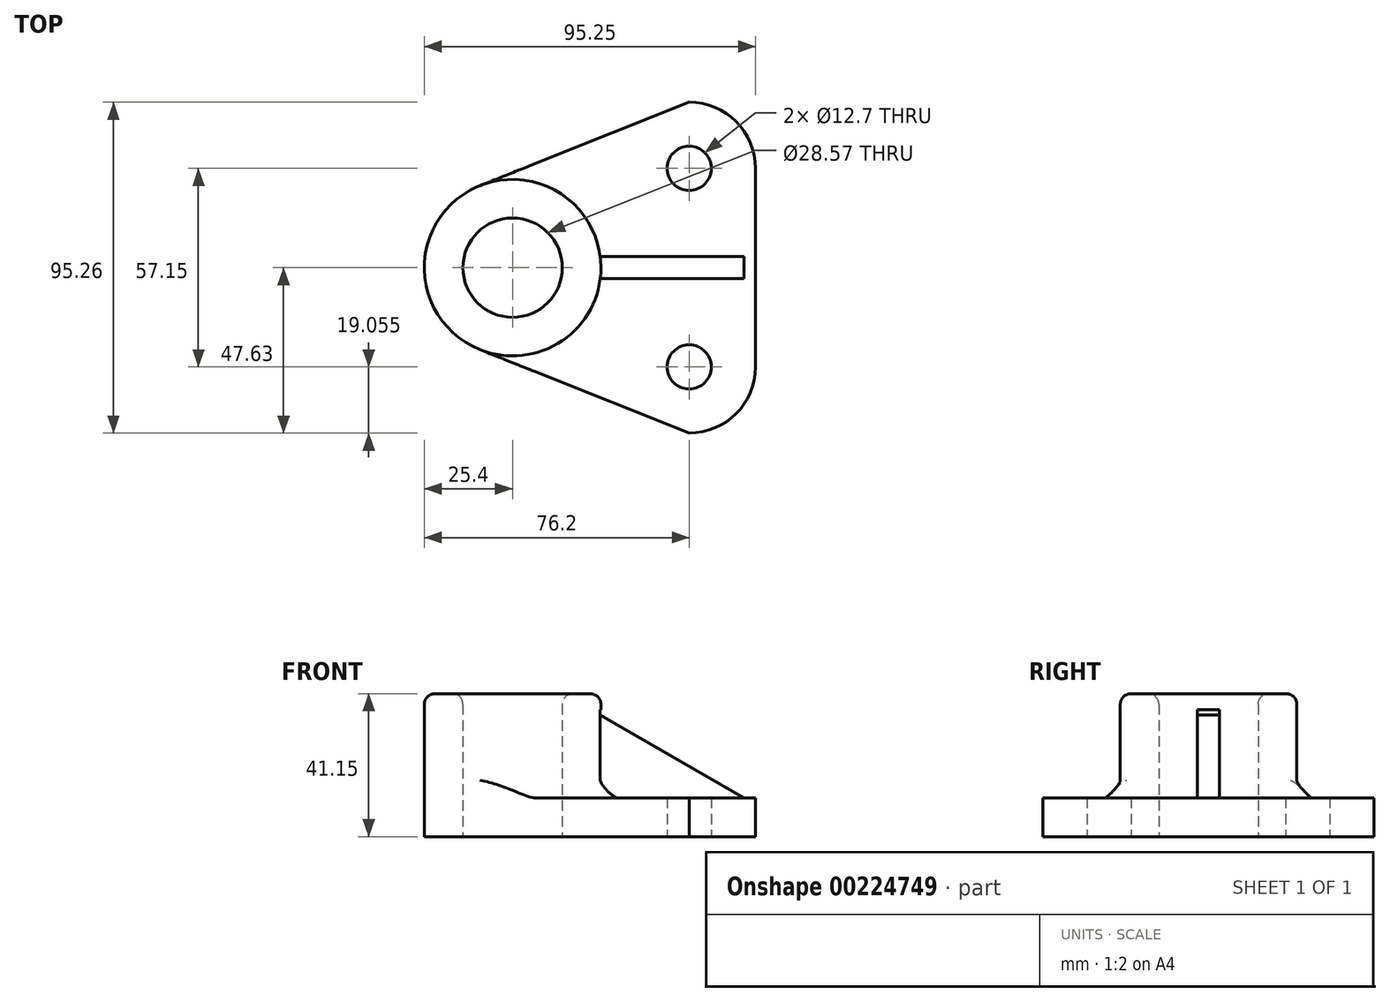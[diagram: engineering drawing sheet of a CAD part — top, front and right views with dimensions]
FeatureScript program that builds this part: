
annotation { "Feature Type Name" : "Feature", "Feature Type Description" : "" }
export const myFeature = defineFeature(function(context is Context, id is Id, definition is map)
    precondition{}
    {
        {
            var Q0;
            Q0=qCreatedBy(makeId("Top.planeOp"),FACE);
            var sketch = newSketch(context, id + "F0", { "sketchPlane" : qUnion([Q0])});
            skCircle(sketch, "E0", {"center": v(0, 0) * mm, "radius": 25.4 * mm});
            skCircle(sketch, "E1", {"center": v(50.8, -28.58) * mm, "radius": 6.35 * mm});
            skCircle(sketch, "E2", {"center": v(50.8, 28.57) * mm, "radius": 6.35 * mm});
            skArc(sketch, "E3", {"start": v(69.85, 28.57) * mm, "mid": v(64.27, 42.05) * mm, "end": v(50.8, 47.62) * mm});
            skArc(sketch, "E4", {"start": v(50.8, -47.62) * mm, "mid": v(64.27, -42.05) * mm, "end": v(69.85, -28.58) * mm});
            skLineSegment(sketch, "E5", {"start": v(69.85, 28.57) * mm, "end": v(69.85, -28.58) * mm});
            skLineSegment(sketch, "E6", {"start": v(0, 0) * mm, "end": v(0, 25.4) * mm});
            skLineSegment(sketch, "E7", {"start": v(0, 0) * mm, "end": v(0, -25.4) * mm});
            skLineSegment(sketch, "E8", {"start": v(50.8, 47.62) * mm, "end": v(-9.42, 23.6) * mm});
            skLineSegment(sketch, "E9", {"start": v(50.8, -47.63) * mm, "end": v(-9.42, -23.6) * mm});
            skCircle(sketch, "E10", {"center": v(0, 0) * mm, "radius": 14.29 * mm});
            skLineSegment(sketch, "E11", {"start": v(69.85, 0) * mm, "end": v(66.55, 0) * mm});
            skPoint(sketch, "E11.endSnap0", {"position": v(69.85, 0) * mm});
            skLineSegment(sketch, "E12.right", {"start": v(108.5, -2.46) * mm, "end": v(108.5, 2.46) * mm});
            skPoint(sketch, "E12.middle", {"position": v(66.55, 0) * mm});
            skPoint(sketch, "E13.orphan", {"position": v(24.6, -2.46) * mm});
            skPoint(sketch, "E14.orphan", {"position": v(24.6, 2.46) * mm});
            skSolve(sketch);
        }
        {
            var Q0;
            {var subQ0=sQuery(id+"F0.wireOp",EDGE,"E6");var subQ1=sQuery(id+"F0.wireOp",EDGE,"E0");var subQ2=makeQuery(id+"F0.imprint","INTERSECT",VERTEX,{"derivedFrom":[subQ1,subQ0]});Q0=makeQuery(id+"F0.imprint","IMPRINT",FACE,{"disambiguationData":[TD([[makeQuery(id+"F0.imprint","IMPRINT",EDGE,{"disambiguationData":[TD([[subQ2,-1.0]])],"derivedFrom":subQ1}),1.0]])]});}
            var Q1;
            {var subQ0=sQuery(id+"F0.wireOp",EDGE,"E6");var subQ1=sQuery(id+"F0.wireOp",EDGE,"E0");var subQ2=makeQuery(id+"F0.imprint","INTERSECT",VERTEX,{"derivedFrom":[subQ1,subQ0]});Q1=makeQuery(id+"F0.imprint","IMPRINT",FACE,{"disambiguationData":[TD([[makeQuery(id+"F0.imprint","IMPRINT",EDGE,{"disambiguationData":[TD([[subQ2,1.0]])],"derivedFrom":subQ1}),1.0]])]});}
            extrude(context, id + "F1", {"entities" : qUnion([Q0, Q1]), "depth" : 41.15 * mm});
        }
        {
            var Q0;
            Q0 = qSketchRegion(id + "F0", true);
            extrude(context, id + "F2", {"entities" : qUnion([Q0]), "operationType" : NewBodyOperationType.ADD, "depth" : 11.18 * mm});
        }
        {
            var Q0;
            Q0=makeQuery(id+"F1.opExtrude","CAP_FACE",FACE,{"disambiguationData":[OSD([sQuery(id+"F0.wireOp",EDGE,"E0"),sQuery(id+"F0.wireOp",EDGE,"E10")])],"isStart":false});
            fillet(context, id + "F3", {"entities" : qUnion([Q0]), "radius" : 3.05 * mm, "tangentPropagation" : true, "allowEdgeOverflow" : false});
        }
        {
            var Q0;
            Q0=makeQuery(id+"F2.opExtrude","CAP_FACE",FACE,{"disambiguationData":[OSD([sQuery(id+"F0.wireOp",EDGE,"E0"),sQuery(id+"F0.wireOp",EDGE,"E1"),sQuery(id+"F0.wireOp",EDGE,"E2"),sQuery(id+"F0.wireOp",EDGE,"E3"),sQuery(id+"F0.wireOp",EDGE,"E4"),sQuery(id+"F0.wireOp",EDGE,"E5"),sQuery(id+"F0.wireOp",EDGE,"E6"),sQuery(id+"F0.wireOp",EDGE,"E7"),sQuery(id+"F0.wireOp",EDGE,"E8"),sQuery(id+"F0.wireOp",EDGE,"E9"),sQuery(id+"F0.wireOp",EDGE,"E10")])],"isStart":false});
            var sketch = newSketch(context, id + "F4", { "sketchPlane" : qUnion([Q0])});
            skLineSegment(sketch, "E15", {"start": v(69.85, 0) * mm, "end": v(66.55, 0) * mm});
            skPoint(sketch, "E15.endSnap0", {"position": v(69.85, 0) * mm});
            skLineSegment(sketch, "E16.bottom", {"start": v(25.2, -3.17) * mm, "end": v(66.55, -3.17) * mm});
            skLineSegment(sketch, "E16.top", {"start": v(25.2, 3.18) * mm, "end": v(66.55, 3.18) * mm});
            skPoint(sketch, "E16.middle", {"position": v(66.55, 0) * mm});
            skLineSegment(sketch, "E17", {"start": v(66.55, 0) * mm, "end": v(66.55, 3.18) * mm});
            skLineSegment(sketch, "E18", {"start": v(66.55, 0) * mm, "end": v(66.55, -3.17) * mm});
            skPoint(sketch, "E19.start.orphan", {"position": v(25.4, 0) * mm});
            skSolve(sketch);
        }
        {
            var Q0;
            {var subQ1=sQuery(id+"F4.wireOp",EDGE,"E16.bottom");Q0=makeQuery(id+"F4.imprint","IMPRINT",FACE,{"disambiguationData":[TD([[makeQuery(id+"F4.imprint","IMPRINT",EDGE,{"derivedFrom":subQ1}),1.0]])]});}
            extrude(context, id + "F5", {"entities" : qUnion([Q0]), "operationType" : NewBodyOperationType.ADD, "depth" : 25.4 * mm});
        }
        {
            var Q0;
            Q0=makeQuery(id+"F5.opExtrude","SWEPT_FACE",FACE,{"disambiguationData":[OSD([sQuery(id+"F4.wireOp",EDGE,"E16.bottom")])]});
            var sketch = newSketch(context, id + "F6", { "sketchPlane" : qUnion([Q0])});
            skLineSegment(sketch, "E20", {"start": v(66.55, 11.18) * mm, "end": v(25.2, 35.05) * mm});
            skLineSegment(sketch, "E21", {"start": v(66.55, 11.18) * mm, "end": v(66.55, 36.58) * mm});
            skLineSegment(sketch, "E22", {"start": v(66.55, 36.58) * mm, "end": v(25.2, 36.58) * mm});
            skLineSegment(sketch, "E23", {"start": v(25.2, 36.58) * mm, "end": v(25.2, 35.05) * mm});
            skSolve(sketch);
        }
        {
            var Q0;
            Q0=makeQuery(id+"F6.imprint","IMPRINT",FACE,{"disambiguationData":[TD([[makeQuery(id+"F6.imprint","IMPRINT",EDGE,{"derivedFrom":sQuery(id+"F6.wireOp",EDGE,"E20")}),-1.0]])]});
            extrude(context, id + "F7", {"entities" : qUnion([Q0]), "operationType" : NewBodyOperationType.REMOVE, "endBound" : BoundingType.THROUGH_ALL, "oppositeDirection" : true, "depth" : 25.4 * mm});
        }
        {
            var Q0;
            {var subQ0=sQuery(id+"F0.wireOp",EDGE,"E0");var subQ1=makeQuery(id+"F1.opExtrude","SWEPT_FACE",FACE,{"disambiguationData":[OSD([subQ0])]});var subQ2=sQuery(id+"F0.wireOp",EDGE,"E8");var subQ3=makeQuery(id+"F2.opExtrude","CAP_FACE",FACE,{"disambiguationData":[OSD([subQ0,sQuery(id+"F0.wireOp",EDGE,"E1"),sQuery(id+"F0.wireOp",EDGE,"E2"),sQuery(id+"F0.wireOp",EDGE,"E3"),sQuery(id+"F0.wireOp",EDGE,"E4"),sQuery(id+"F0.wireOp",EDGE,"E5"),sQuery(id+"F0.wireOp",EDGE,"E6"),sQuery(id+"F0.wireOp",EDGE,"E7"),subQ2,sQuery(id+"F0.wireOp",EDGE,"E9"),sQuery(id+"F0.wireOp",EDGE,"E10")])],"isStart":false});Q0=makeQuery(id+"F5.boolean.opBoolean","SPLIT",EDGE,{"disambiguationData":[TD([makeQuery(id+"F2.opExtrude","SWEPT_FACE",FACE,{"disambiguationData":[OSD([subQ2])]})])],"derivedFrom":makeQuery(id+"F2.boolean.opBoolean","INTERSECT",EDGE,{"derivedFrom":[subQ1,subQ3]})});}
            fillet(context, id + "F8", {"entities" : qUnion([Q0]), "radius" : 5.08 * mm, "rho" : 0.2, "crossSection" : FilletCrossSection.CONIC, "allowEdgeOverflow" : false});
        }
        {
            var Q0;
            {var subQ0=sQuery(id+"F0.wireOp",EDGE,"E0");var subQ1=makeQuery(id+"F1.opExtrude","SWEPT_FACE",FACE,{"disambiguationData":[OSD([subQ0])]});var subQ2=sQuery(id+"F0.wireOp",EDGE,"E9");var subQ3=makeQuery(id+"F2.opExtrude","CAP_FACE",FACE,{"disambiguationData":[OSD([subQ0,sQuery(id+"F0.wireOp",EDGE,"E1"),sQuery(id+"F0.wireOp",EDGE,"E2"),sQuery(id+"F0.wireOp",EDGE,"E3"),sQuery(id+"F0.wireOp",EDGE,"E4"),sQuery(id+"F0.wireOp",EDGE,"E5"),sQuery(id+"F0.wireOp",EDGE,"E6"),sQuery(id+"F0.wireOp",EDGE,"E7"),sQuery(id+"F0.wireOp",EDGE,"E8"),subQ2,sQuery(id+"F0.wireOp",EDGE,"E10")])],"isStart":false});Q0=makeQuery(id+"F5.boolean.opBoolean","SPLIT",EDGE,{"disambiguationData":[TD([makeQuery(id+"F2.opExtrude","SWEPT_FACE",FACE,{"disambiguationData":[OSD([subQ2])]})])],"derivedFrom":makeQuery(id+"F2.boolean.opBoolean","INTERSECT",EDGE,{"derivedFrom":[subQ1,subQ3]})});}
            fillet(context, id + "F9", {"entities" : qUnion([Q0]), "radius" : 5.08 * mm, "tangentPropagation" : true, "rho" : .20, "crossSection" : FilletCrossSection.CONIC, "allowEdgeOverflow" : false});
        }
    });
